# Revit family: BLAUBERG-KOMFORT_EC_DBW_3000
name_source: partatom
category: Mechanical Equipment
units: mm (PartAtom-declared; Revit-internal decimal feet)

## family parameters
Always vertical = Yes
Classification = None
Cut with Voids When Loaded = No
OmniClass Number = 23.75.35.14
OmniClass Title = Air Handling Units
Part Type = Normal
Room Calculation Point = No
Round Connector Dimension = Use Diameter
Shared = No
Work Plane-Based = No

## types (1)
- KOMFORT EC DBW 3000 S21
    B = 1265 mm  [stored 4.15026 ft]
    B1 = 347 mm  [stored 1.13845 ft]
    B2 = 347 mm  [stored 1.13845 ft]
    Bottom Maintenance Zone Height = 600 mm  [stored 1.9685 ft]
    Casing Material = Metal Zinc
    Current = 4 A
    D = 400 mm  [stored 1.31234 ft]
    DPS_B1 = 460 mm  [stored 1.50919 ft]
    DPS_B2 = 450 mm  [stored 1.47638 ft]
    DPS_H = 123 mm  [stored 0.403543 ft]
    Description = Air Handling Unit
    Drain Connection Diameter = 16 mm  [stored 0.0524934 ft]
    DrainD = 16 mm  [stored 0.0524934 ft]
    DrainPipe = Yes
    Duct Connection Diameter = 400 mm  [stored 1.31234 ft]
    Extract Air Filter = G4
    Family Version = 1.0
    H = 881 mm  [stored 2.89042 ft]
    H1 = 427 mm  [stored 1.40092 ft]
    HDrainCon = 36 mm  [stored 0.11811 ft]
    HandleB = 100 mm  [stored 0.328084 ft]
    HandleL1 = 408 mm
    HandleL2 = 509 mm  [stored 1.66995 ft]
    Heat Exchanger Material = aluminium
    Heat Exchanger Type = cross-flow
    Heat recovery efficiency (%) = 59..72
    Heater Connection Diameter = 25 mm  [stored 0.082021 ft]
    HeaterReturnConH = 590 mm  [stored 1.9357 ft]
    HeaterReturnConL = 546 mm  [stored 1.79134 ft]
    HeaterSupplyConH = 290 mm  [stored 0.951444 ft]
    HeaterSupplyConL = 589 mm
    L = 1835 mm  [stored 6.02034 ft]
    LDrainCon = 35 mm  [stored 0.114829 ft]
    LDrainCon1 = 710 mm
    LDuctCon = 50 mm  [stored 0.164042 ft]
    Load Classification = HVAC
    Maintenance Zone Material = Maintenance Zone
    Manufacturer = Blauberg
    Maximum Air Flow = 4300 m³/h
    Maximum Unit Current = 4 A
    Maximum Unit Power = 2226 W
    Model = KOMFORT EC DBW 3000 S21
    Number of Poles = 3
    Plastic Material = Polypropylene Black
    Power = 2226 W
    Power Factor = 1
    RPM (min-1) = 3400
    SEC Class = NRVU
    Side Maintenance Zone Height = 850 mm  [stored 2.78871 ft]
    Sound Pressure Level at 3 m (dBA) = 46
    Supply Air Filter = G4
    Transported Air Temperature (°C) = -25…+40
    Type Comments = Air Handling Unit KOMFORT EC DBW 3000 S21
    URL = https://blaubergventilatoren.de
    Voltage = 400 V
    Weight = 268.00 kg

note: [stored X ft] marks values corroborated as IEEE doubles in the binary element streams (Revit-internal decimal feet)

## geometry (parser evidence)
native form markers: Sweep x5
no freeform markers — native parametric forms only
